# Revit family: Cable_Tray_Support-OBO_Bettermann-Barrier_Strip_TSG
name_source: partatom
category: Specialty Equipment
revit_build: Autodesk Revit MEP 2012 (Build: 20110309_2315(x64)
units: mm (PartAtom-declared; Revit-internal decimal feet)

## types (2) — shared parameters
Assembly Code = D5030600
Classification = Refer to online Catalog for UL and cUL classifed sizes and wire sizes.
Description = Barrier strip
Height = 60 mm  [stored 0.19685 ft]
Manufacturer = OBO Bettermann
Model = MKS
Product Page URL = http://catalog2.obo-bettermann.com
URL = http://www.obo-bettermann.com
zero-valued in all types: Default Elevation

## per-type parameters (varying)
| type | Support Material |
| Strip Galvanised | Metal - OBO Bettermann - Strip-Galvanised |
| Hot Dipped Galvanised | Metal - OBO Bettermann - Hot-Dipped-Galvanised |

note: [stored X ft] marks values corroborated as IEEE doubles in the binary element streams (Revit-internal decimal feet)

## geometry (parser evidence)
native form markers: Blend x3, Sweep x6
no freeform markers — native parametric forms only
